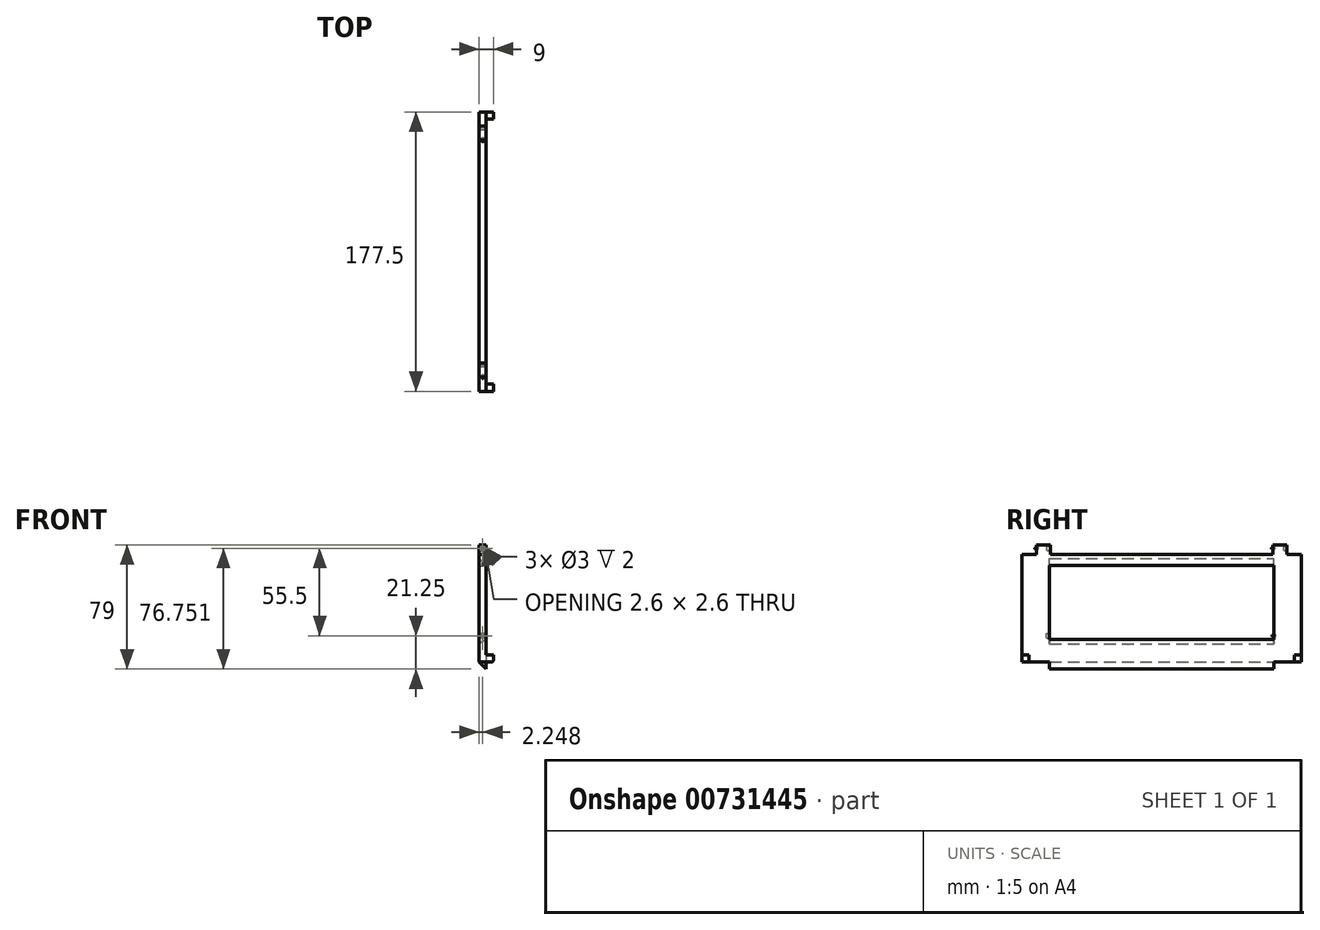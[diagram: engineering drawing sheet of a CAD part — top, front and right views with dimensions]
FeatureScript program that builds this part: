
annotation { "Feature Type Name" : "Feature", "Feature Type Description" : "" }
export const myFeature = defineFeature(function(context is Context, id is Id, definition is map)
    precondition{}
    {
        {
            var Q0;
            Q0=qCreatedBy(makeId("Front.planeOp"),FACE);
            var sketch = newSketch(context, id + "F0", { "sketchPlane" : qUnion([Q0])});
            skLineSegment(sketch, "E0", {"start": v(-40.86, 100.77) * mm, "end": v(-36.36, 100.77) * mm});
            skLineSegment(sketch, "E1", {"start": v(-36.36, 100.77) * mm, "end": v(-36.36, 30.77) * mm});
            skLineSegment(sketch, "E2", {"start": v(-36.36, 30.77) * mm, "end": v(-31.86, 30.77) * mm});
            skLineSegment(sketch, "E3", {"start": v(-31.86, 30.77) * mm, "end": v(-31.86, 27.27) * mm});
            skLineSegment(sketch, "E4", {"start": v(-32.86, 26.27) * mm, "end": v(-36.36, 26.27) * mm});
            skCircle(sketch, "E5", {"center": v(-38.61, 98.52) * mm, "radius": 1.3 * mm});
            skCircle(sketch, "E6", {"center": v(-38.61, 98.52) * mm, "radius": 1.5 * mm});
            skCircle(sketch, "E7", {"center": v(-38.61, 43.02) * mm, "radius": 1.5 * mm});
            skCircle(sketch, "E8", {"center": v(-38.61, 43.02) * mm, "radius": 1.3 * mm});
            skLineSegment(sketch, "E9", {"start": v(-40.86, 94.77) * mm, "end": v(-36.36, 94.77) * mm});
            skLineSegment(sketch, "E10", {"start": v(-36.36, 87.52) * mm, "end": v(-40.86, 92.02) * mm});
            skLineSegment(sketch, "E11", {"start": v(-36.36, 40.52) * mm, "end": v(-40.86, 37.92) * mm});
            skPoint(sketch, "E12.visualSharp", {"position": v(-31.86, 26.27) * mm});
            skArc(sketch, "E12.filletArc", {"start": v(-32.86, 26.27) * mm, "mid": v(-32.16, 26.56) * mm, "end": v(-31.86, 27.27) * mm});
            skLineSegment(sketch, "E13", {"start": v(-36.36, 30.77) * mm, "end": v(-36.36, 26.27) * mm});
            skLineSegment(sketch, "E14", {"start": v(-36.36, 26.27) * mm, "end": v(-40.86, 26.27) * mm});
            skLineSegment(sketch, "E15", {"start": v(-36.36, 26.27) * mm, "end": v(-36.36, 21.77) * mm});
            skLineSegment(sketch, "E16", {"start": v(-36.36, 21.77) * mm, "end": v(-40.86, 26.27) * mm});
            skLineSegment(sketch, "E17", {"start": v(-40.86, 26.27) * mm, "end": v(-40.86, 100.77) * mm});
            skSolve(sketch);
        }
        {
            var Q0;
            {var subQ1=sQuery(id+"F0.wireOp",EDGE,"E0");Q0=makeQuery(id+"F0.imprint","IMPRINT",FACE,{"disambiguationData":[TD([[makeQuery(id+"F0.imprint","IMPRINT",EDGE,{"derivedFrom":subQ1}),-1.0]])]});}
            var Q1;
            {var subQ0=sQuery(id+"F0.wireOp",EDGE,"E9");Q1=makeQuery(id+"F0.imprint","IMPRINT",FACE,{"disambiguationData":[TD([[makeQuery(id+"F0.imprint","IMPRINT",EDGE,{"derivedFrom":subQ0}),-1.0]])]});}
            var Q2;
            Q2=makeQuery(id+"F0.imprint","IMPRINT",FACE,{"disambiguationData":[TD([[makeQuery(id+"F0.imprint","IMPRINT",EDGE,{"derivedFrom":sQuery(id+"F0.wireOp",EDGE,"E7")}),-1.0]])]});
            var Q3;
            {var subQ0=sQuery(id+"F0.wireOp",EDGE,"E11");Q3=makeQuery(id+"F0.imprint","IMPRINT",FACE,{"disambiguationData":[TD([[makeQuery(id+"F0.imprint","IMPRINT",EDGE,{"derivedFrom":subQ0}),1.0]])]});}
            var Q4;
            Q4=makeQuery(id+"F0.imprint","IMPRINT",FACE,{"disambiguationData":[TD([[makeQuery(id+"F0.imprint","IMPRINT",EDGE,{"derivedFrom":sQuery(id+"F0.wireOp",EDGE,"E2")}),-1.0]])]});
            extrude(context, id + "F1", {"entities" : qUnion([Q0, Q1, Q2, Q3, Q4]), "depth" : 177.5 * mm, "offsetDistance" : 25 * mm});
        }
        {
            var Q0;
            {var subQ1=sQuery(id+"F0.wireOp",EDGE,"E0");Q0=makeQuery(id+"F0.imprint","IMPRINT",FACE,{"disambiguationData":[TD([[makeQuery(id+"F0.imprint","IMPRINT",EDGE,{"derivedFrom":subQ1}),-1.0]])]});}
            extrude(context, id + "F2", {"entities" : qUnion([Q0]), "operationType" : NewBodyOperationType.REMOVE, "depth" : 177.5 * mm, "offsetDistance" : 25 * mm});
        }
        {
            var Q0;
            {var subQ1=sQuery(id+"F0.wireOp",EDGE,"E0");Q0=makeQuery(id+"F0.imprint","IMPRINT",FACE,{"disambiguationData":[TD([[makeQuery(id+"F0.imprint","IMPRINT",EDGE,{"derivedFrom":subQ1}),-1.0]])]});}
            extrude(context, id + "F3", {"entities" : qUnion([Q0]), "operationType" : NewBodyOperationType.ADD, "depth" : 168.3 * mm, "offsetDistance" : 25 * mm});
        }
        {
            var Q0;
            {var subQ1=sQuery(id+"F0.wireOp",EDGE,"E0");Q0=makeQuery(id+"F0.imprint","IMPRINT",FACE,{"disambiguationData":[TD([[makeQuery(id+"F0.imprint","IMPRINT",EDGE,{"derivedFrom":subQ1}),-1.0]])]});}
            extrude(context, id + "F4", {"entities" : qUnion([Q0]), "operationType" : NewBodyOperationType.REMOVE, "depth" : 159.5 * mm, "offsetDistance" : 25 * mm});
        }
        {
            var Q0;
            {var subQ1=sQuery(id+"F0.wireOp",EDGE,"E0");Q0=makeQuery(id+"F0.imprint","IMPRINT",FACE,{"disambiguationData":[TD([[makeQuery(id+"F0.imprint","IMPRINT",EDGE,{"derivedFrom":subQ1}),-1.0]])]});}
            extrude(context, id + "F5", {"entities" : qUnion([Q0]), "operationType" : NewBodyOperationType.ADD, "depth" : 18 * mm, "offsetDistance" : 25 * mm});
        }
        {
            var Q0;
            {var subQ1=sQuery(id+"F0.wireOp",EDGE,"E0");Q0=makeQuery(id+"F0.imprint","IMPRINT",FACE,{"disambiguationData":[TD([[makeQuery(id+"F0.imprint","IMPRINT",EDGE,{"derivedFrom":subQ1}),-1.0]])]});}
            extrude(context, id + "F6", {"entities" : qUnion([Q0]), "operationType" : NewBodyOperationType.REMOVE, "depth" : 9.2 * mm, "offsetDistance" : 25 * mm});
        }
        {
            var Q0;
            Q0=makeQuery(id+"F0.imprint","IMPRINT",FACE,{"disambiguationData":[TD([[makeQuery(id+"F0.imprint","IMPRINT",EDGE,{"derivedFrom":sQuery(id+"F0.wireOp",EDGE,"E7")}),-1.0]])]});
            extrude(context, id + "F7", {"entities" : qUnion([Q0]), "operationType" : NewBodyOperationType.REMOVE, "depth" : 159.9 * mm, "offsetDistance" : 25 * mm});
        }
        {
            var Q0;
            Q0=makeQuery(id+"F0.imprint","IMPRINT",FACE,{"disambiguationData":[TD([[makeQuery(id+"F0.imprint","IMPRINT",EDGE,{"derivedFrom":sQuery(id+"F0.wireOp",EDGE,"E7")}),-1.0]])]});
            extrude(context, id + "F8", {"entities" : qUnion([Q0]), "operationType" : NewBodyOperationType.ADD, "depth" : 17.6 * mm, "offsetDistance" : 25 * mm});
        }
        {
            var Q0;
            Q0=makeQuery(id+"F0.imprint","IMPRINT",FACE,{"disambiguationData":[TD([[makeQuery(id+"F0.imprint","IMPRINT",EDGE,{"derivedFrom":sQuery(id+"F0.wireOp",EDGE,"E2")}),-1.0]])]});
            extrude(context, id + "F9", {"entities" : qUnion([Q0]), "operationType" : NewBodyOperationType.REMOVE, "depth" : 173 * mm, "offsetDistance" : 25 * mm});
        }
        {
            var Q0;
            Q0=makeQuery(id+"F0.imprint","IMPRINT",FACE,{"disambiguationData":[TD([[makeQuery(id+"F0.imprint","IMPRINT",EDGE,{"derivedFrom":sQuery(id+"F0.wireOp",EDGE,"E2")}),-1.0]])]});
            extrude(context, id + "F10", {"entities" : qUnion([Q0]), "operationType" : NewBodyOperationType.ADD, "depth" : 4.5 * mm, "offsetDistance" : 25 * mm});
        }
        {
            var Q0;
            Q0=makeQuery(id+"F0.imprint","IMPRINT",FACE,{"disambiguationData":[TD([[makeQuery(id+"F0.imprint","IMPRINT",EDGE,{"derivedFrom":sQuery(id+"F0.wireOp",EDGE,"E14")}),1.0]])]});
            extrude(context, id + "F11", {"entities" : qUnion([Q0]), "operationType" : NewBodyOperationType.ADD, "depth" : 159.9 * mm, "offsetDistance" : 25 * mm});
        }
        {
            var Q0;
            Q0=makeQuery(id+"F0.imprint","IMPRINT",FACE,{"disambiguationData":[TD([[makeQuery(id+"F0.imprint","IMPRINT",EDGE,{"derivedFrom":sQuery(id+"F0.wireOp",EDGE,"E14")}),1.0]])]});
            extrude(context, id + "F12", {"entities" : qUnion([Q0]), "operationType" : NewBodyOperationType.REMOVE, "depth" : 17.6 * mm, "offsetDistance" : 25 * mm});
        }
        {
            var Q0;
            Q0=makeQuery(id+"F6.boolean.opBoolean","COPY",FACE,{"derivedFrom":makeQuery(id+"F6.opExtrude","CAP_FACE",FACE,{"disambiguationData":[OSD([sQuery(id+"F0.wireOp",EDGE,"E0"),sQuery(id+"F0.wireOp",EDGE,"7984388c-d5ee-4428-ac95-fbeddbd0fe1a"),sQuery(id+"F0.wireOp",EDGE,"E1"),sQuery(id+"F0.wireOp",EDGE,"E6"),sQuery(id+"F0.wireOp",EDGE,"E9")])],"isStart":false})});
            var sketch = newSketch(context, id + "F13", { "sketchPlane" : qUnion([Q0])});
            skCircle(sketch, "E18", {"center": v(38.61, 98.52) * mm, "radius": 1.3 * mm});
            skCircle(sketch, "E19", {"center": v(38.61, 98.52) * mm, "radius": 1.5 * mm});
            skSolve(sketch);
        }
        {
            var Q0;
            Q0=makeQuery(id+"F4.boolean.opBoolean","COPY",FACE,{"derivedFrom":makeQuery(id+"F4.opExtrude","CAP_FACE",FACE,{"disambiguationData":[OSD([sQuery(id+"F0.wireOp",EDGE,"E0"),sQuery(id+"F0.wireOp",EDGE,"7984388c-d5ee-4428-ac95-fbeddbd0fe1a"),sQuery(id+"F0.wireOp",EDGE,"E1"),sQuery(id+"F0.wireOp",EDGE,"E6"),sQuery(id+"F0.wireOp",EDGE,"E9")])],"isStart":false})});
            var sketch = newSketch(context, id + "F14", { "sketchPlane" : qUnion([Q0])});
            skCircle(sketch, "E20", {"center": v(38.61, 98.52) * mm, "radius": 1.3 * mm});
            skCircle(sketch, "E21", {"center": v(38.61, 98.52) * mm, "radius": 1.5 * mm});
            skSolve(sketch);
        }
        {
            var Q0;
            {var subQ0=sQuery(id+"F0.wireOp",EDGE,"E14");var subQ1=sQuery(id+"F0.wireOp",EDGE,"7984388c-d5ee-4428-ac95-fbeddbd0fe1a");var subQ2=sQuery(id+"F0.wireOp",EDGE,"E12.filletArc");var subQ3=sQuery(id+"F0.wireOp",EDGE,"E4");var subQ4=sQuery(id+"F0.wireOp",EDGE,"E3");var subQ5=sQuery(id+"F0.wireOp",EDGE,"E2");var subQ6=sQuery(id+"F0.wireOp",EDGE,"E11");var subQ7=sQuery(id+"F0.wireOp",EDGE,"E10");var subQ8=sQuery(id+"F0.wireOp",EDGE,"E7");var subQ9=sQuery(id+"F0.wireOp",EDGE,"E1");var subQ16=sQuery(id+"F0.wireOp",EDGE,"E9");var subQ17=sQuery(id+"F0.wireOp",EDGE,"E6");var subQ18=sQuery(id+"F0.wireOp",EDGE,"E0");var subQ19=makeQuery(id+"F5.boolean.opBoolean","MERGE",FACE,{"derivedFrom":[makeQuery(id+"F3.boolean.opBoolean","MERGE",FACE,{"derivedFrom":[makeQuery(id+"F1.opExtrude","CAP_FACE",FACE,{"disambiguationData":[OSD([subQ18,subQ1,subQ9,subQ5,subQ4,subQ3,subQ17,subQ8,subQ2,subQ0])],"isStart":true}),makeQuery(id+"F3.opExtrude","CAP_FACE",FACE,{"disambiguationData":[OSD([subQ18,subQ1,subQ9,subQ17,subQ16])],"isStart":true})]}),makeQuery(id+"F5.opExtrude","CAP_FACE",FACE,{"disambiguationData":[OSD([subQ18,subQ1,subQ9,subQ17,subQ16])],"isStart":true})]});Q0=makeQuery(id+"F11.boolean.opBoolean","MERGE",FACE,{"derivedFrom":[makeQuery(id+"F10.boolean.opBoolean","MERGE",FACE,{"derivedFrom":[makeQuery(id+"F8.boolean.opBoolean","MERGE",FACE,{"derivedFrom":[makeQuery(id+"F7.boolean.opBoolean","SPLIT",FACE,{"disambiguationData":[TD([makeQuery(id+"F1.opExtrude","SWEPT_FACE",FACE,{"disambiguationData":[OSD([subQ5])]})])],"derivedFrom":subQ19}),makeQuery(id+"F7.boolean.opBoolean","SPLIT",FACE,{"disambiguationData":[TD([makeQuery(id+"F6.boolean.opBoolean","COPY",FACE,{"derivedFrom":makeQuery(id+"F6.opExtrude","SWEPT_FACE",FACE,{"disambiguationData":[OSD([subQ16])]})})])],"derivedFrom":subQ19}),makeQuery(id+"F8.opExtrude","CAP_FACE",FACE,{"disambiguationData":[OSD([subQ1,subQ9,subQ8,subQ7,subQ6])],"isStart":true})]}),makeQuery(id+"F10.opExtrude","CAP_FACE",FACE,{"disambiguationData":[OSD([subQ5,subQ4,subQ3,subQ2,sQuery(id+"F0.wireOp",EDGE,"E13")])],"isStart":true})]}),makeQuery(id+"F11.opExtrude","CAP_FACE",FACE,{"disambiguationData":[OSD([subQ1,sQuery(id+"F0.wireOp",EDGE,"1a4fdf55-8981-4492-bd3b-b7fde15d5d4e"),subQ0])],"isStart":true})]});}
            var sketch = newSketch(context, id + "F15", { "sketchPlane" : qUnion([Q0])});
            skCircle(sketch, "E22", {"center": v(38.61, 43.02) * mm, "radius": 1.5 * mm});
            skCircle(sketch, "E23", {"center": v(38.61, 43.02) * mm, "radius": 1.3 * mm});
            skSolve(sketch);
        }
        {
            var Q0;
            Q0=makeQuery(id+"F7.boolean.opBoolean","COPY",FACE,{"derivedFrom":makeQuery(id+"F7.opExtrude","CAP_FACE",FACE,{"disambiguationData":[OSD([sQuery(id+"F0.wireOp",EDGE,"7984388c-d5ee-4428-ac95-fbeddbd0fe1a"),sQuery(id+"F0.wireOp",EDGE,"E1"),sQuery(id+"F0.wireOp",EDGE,"E7"),sQuery(id+"F0.wireOp",EDGE,"E10"),sQuery(id+"F0.wireOp",EDGE,"E11")])],"isStart":false})});
            var sketch = newSketch(context, id + "F16", { "sketchPlane" : qUnion([Q0])});
            skCircle(sketch, "E24", {"center": v(38.61, 43.02) * mm, "radius": 1.5 * mm});
            skSolve(sketch);
        }
        {
            var Q0;
            Q0=makeQuery(id+"F13.imprint","IMPRINT",FACE,{"disambiguationData":[TD([[makeQuery(id+"F13.imprint","IMPRINT",EDGE,{"derivedFrom":sQuery(id+"F13.wireOp",EDGE,"E18")}),-1.0]])]});
            var Q1;
            Q1=makeQuery(id+"F14.imprint","IMPRINT",FACE,{"disambiguationData":[TD([[makeQuery(id+"F14.imprint","IMPRINT",EDGE,{"derivedFrom":sQuery(id+"F14.wireOp",EDGE,"E20")}),-1.0]])]});
            var Q2;
            Q2=makeQuery(id+"F15.imprint","IMPRINT",FACE,{"disambiguationData":[TD([[makeQuery(id+"F15.imprint","IMPRINT",EDGE,{"derivedFrom":sQuery(id+"F15.wireOp",EDGE,"E22")}),-1.0]])]});
            extrude(context, id + "F17", {"entities" : qUnion([Q0, Q1, Q2]), "operationType" : NewBodyOperationType.ADD, "oppositeDirection" : true, "depth" : 8.8 * mm, "offsetDistance" : 25 * mm});
        }
        {
            var Q0;
            Q0=makeQuery(id+"F13.imprint","IMPRINT",FACE,{"disambiguationData":[TD([[makeQuery(id+"F13.imprint","IMPRINT",EDGE,{"derivedFrom":sQuery(id+"F13.wireOp",EDGE,"E18")}),1.0]])]});
            var Q1;
            Q1=makeQuery(id+"F14.imprint","IMPRINT",FACE,{"disambiguationData":[TD([[makeQuery(id+"F14.imprint","IMPRINT",EDGE,{"derivedFrom":sQuery(id+"F14.wireOp",EDGE,"E20")}),1.0]])]});
            var Q2;
            Q2=makeQuery(id+"F15.imprint","IMPRINT",FACE,{"disambiguationData":[TD([[makeQuery(id+"F15.imprint","IMPRINT",EDGE,{"derivedFrom":sQuery(id+"F15.wireOp",EDGE,"E23")}),1.0]])]});
            extrude(context, id + "F18", {"entities" : qUnion([Q0, Q1, Q2]), "operationType" : NewBodyOperationType.ADD, "oppositeDirection" : true, "depth" : 9.8 * mm, "offsetDistance" : 25 * mm});
        }
        {
            var Q0;
            Q0=makeQuery(id+"F15.imprint","IMPRINT",FACE,{"disambiguationData":[TD([[makeQuery(id+"F15.imprint","IMPRINT",EDGE,{"derivedFrom":sQuery(id+"F15.wireOp",EDGE,"E22")}),-1.0]])]});
            var Q1;
            Q1=makeQuery(id+"F16.imprint","IMPRINT",FACE,{"disambiguationData":[TD([[makeQuery(id+"F16.imprint","IMPRINT",EDGE,{"derivedFrom":sQuery(id+"F16.wireOp",EDGE,"E24")}),-1.0]])]});
            extrude(context, id + "F19", {"entities" : qUnion([Q0, Q1]), "operationType" : NewBodyOperationType.ADD, "oppositeDirection" : true, "depth" : 17.6 * mm, "offsetDistance" : 25 * mm});
        }
        {
            var Q0;
            Q0=makeQuery(id+"F15.imprint","IMPRINT",FACE,{"disambiguationData":[TD([[makeQuery(id+"F15.imprint","IMPRINT",EDGE,{"derivedFrom":sQuery(id+"F15.wireOp",EDGE,"E23")}),1.0]])]});
            extrude(context, id + "F20", {"entities" : qUnion([Q0]), "operationType" : NewBodyOperationType.ADD, "oppositeDirection" : true, "depth" : 18.6 * mm, "offsetDistance" : 25 * mm});
        }
        {
            var Q0;
            Q0=makeQuery(id+"F13.imprint","IMPRINT",FACE,{"disambiguationData":[TD([[makeQuery(id+"F13.imprint","IMPRINT",EDGE,{"derivedFrom":sQuery(id+"F13.wireOp",EDGE,"E18")}),1.0]])]});
            var Q1;
            Q1=makeQuery(id+"F13.imprint","IMPRINT",FACE,{"disambiguationData":[TD([[makeQuery(id+"F13.imprint","IMPRINT",EDGE,{"derivedFrom":sQuery(id+"F13.wireOp",EDGE,"E18")}),-1.0]])]});
            var Q2;
            Q2=makeQuery(id+"F14.imprint","IMPRINT",FACE,{"disambiguationData":[TD([[makeQuery(id+"F14.imprint","IMPRINT",EDGE,{"derivedFrom":sQuery(id+"F14.wireOp",EDGE,"E20")}),1.0]])]});
            var Q3;
            Q3=makeQuery(id+"F14.imprint","IMPRINT",FACE,{"disambiguationData":[TD([[makeQuery(id+"F14.imprint","IMPRINT",EDGE,{"derivedFrom":sQuery(id+"F14.wireOp",EDGE,"E20")}),-1.0]])]});
            var Q4;
            Q4=makeQuery(id+"F16.imprint","IMPRINT",FACE,{"disambiguationData":[TD([[makeQuery(id+"F16.imprint","IMPRINT",EDGE,{"derivedFrom":sQuery(id+"F16.wireOp",EDGE,"E24")}),-1.0]])]});
            extrude(context, id + "F21", {"entities" : qUnion([Q0, Q1, Q2, Q3, Q4]), "operationType" : NewBodyOperationType.REMOVE, "oppositeDirection" : true, "depth" : 2 * mm, "offsetDistance" : 25 * mm});
        }
        {
            var Q0;
            Q0=makeQuery(id+"F18.opExtrude","CAP_EDGE",EDGE,{"disambiguationData":[OSD([sQuery(id+"F13.wireOp",EDGE,"E18")])],"isStart":false});
            var Q1;
            Q1=makeQuery(id+"F20.opExtrude","CAP_EDGE",EDGE,{"disambiguationData":[OSD([sQuery(id+"F15.wireOp",EDGE,"E23")])],"isStart":false});
            var Q2;
            Q2=makeQuery(id+"F18.opExtrude","CAP_EDGE",EDGE,{"disambiguationData":[OSD([sQuery(id+"F14.wireOp",EDGE,"E20")])],"isStart":false});
            fillet(context, id + "F22", {"entities" : qUnion([Q0, Q1, Q2]), "radius" : 1 * mm, "tangentPropagation" : true, "allowEdgeOverflow" : false});
        }
    });
